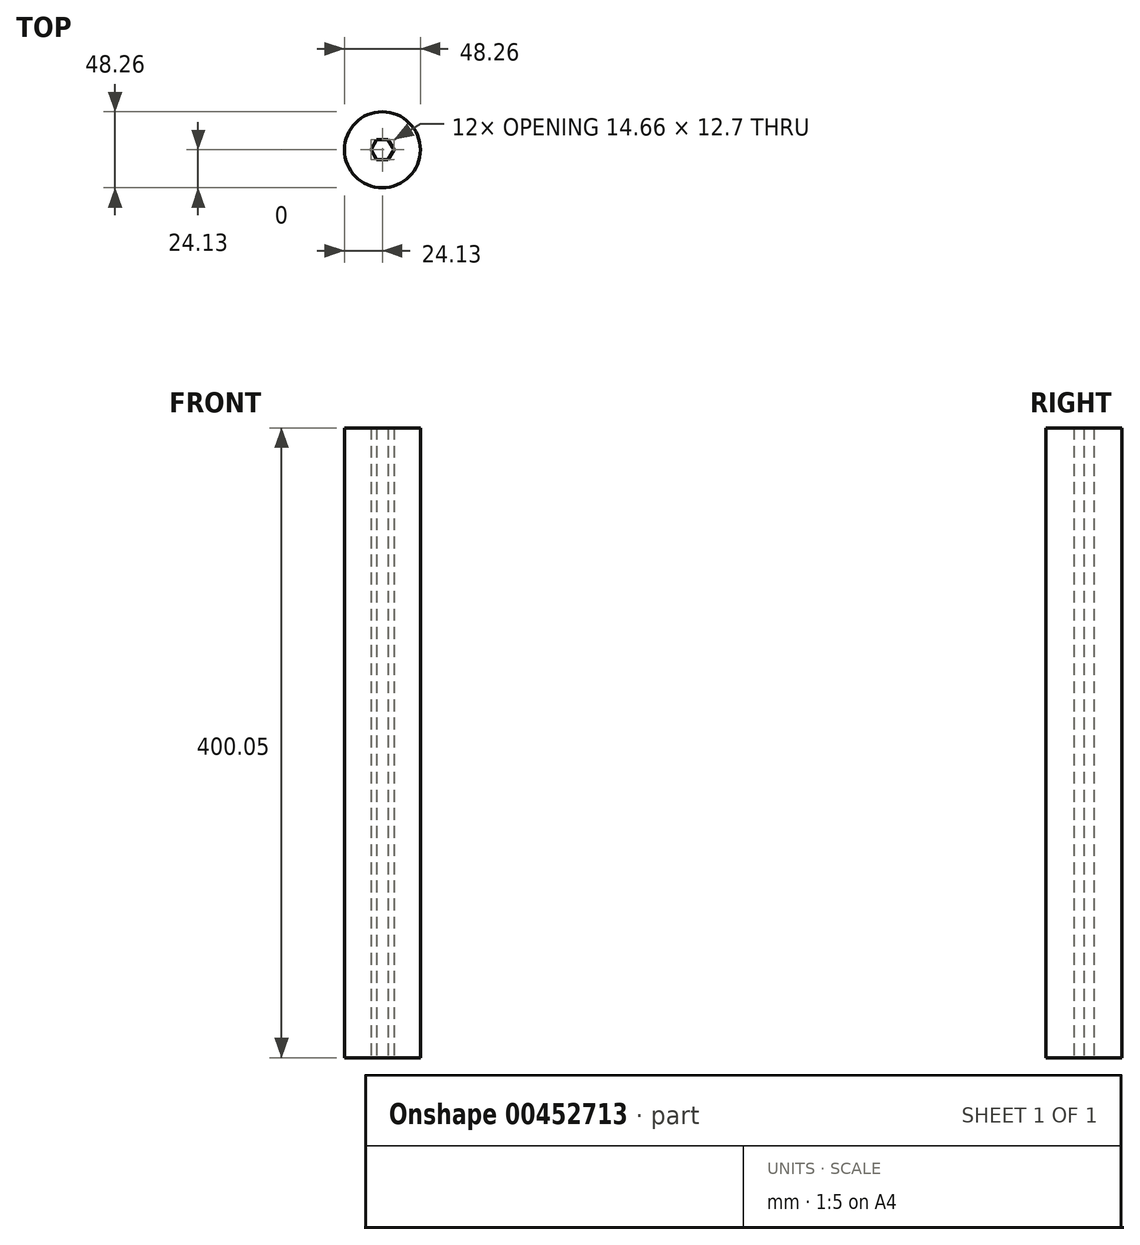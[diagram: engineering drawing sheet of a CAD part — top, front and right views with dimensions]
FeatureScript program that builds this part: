
annotation { "Feature Type Name" : "Feature", "Feature Type Description" : "" }
export const myFeature = defineFeature(function(context is Context, id is Id, definition is map)
    precondition{}
    {
        {
            var Q0;
            Q0=qCreatedBy(makeId("Top.planeOp"),FACE);
            var sketch = newSketch(context, id + "F0", { "sketchPlane" : qUnion([Q0])});
            skCircle(sketch, "E0", {"center": v(0, 0) * mm, "radius": 24.13 * mm});
            skCircle(sketch, "E1.cCircle", {"center": v(0, 0) * mm, "radius": 6.35 * mm, "construction": true});
            skLineSegment(sketch, "E1.0", {"start": v(-3.67, 6.35) * mm, "end": v(3.67, 6.35) * mm});
            skLineSegment(sketch, "E1.1", {"start": v(3.67, 6.35) * mm, "end": v(7.33, 0) * mm});
            skLineSegment(sketch, "E1.2", {"start": v(7.33, 0) * mm, "end": v(3.67, -6.35) * mm});
            skLineSegment(sketch, "E1.3", {"start": v(3.67, -6.35) * mm, "end": v(-3.67, -6.35) * mm});
            skLineSegment(sketch, "E1.4", {"start": v(-3.67, -6.35) * mm, "end": v(-7.33, 0) * mm});
            skLineSegment(sketch, "E1.5", {"start": v(-7.33, 0) * mm, "end": v(-3.67, 6.35) * mm});
            skPoint(sketch, "E1.0.midPoint", {"position": v(0, 6.35) * mm});
            skSolve(sketch);
        }
        {
            var Q0;
            Q0 = qSketchRegion(id + "F0", true);
            extrude(context, id + "F1", {"entities" : qUnion([Q0]), "depth" : 400.05 * mm, "offsetDistance" : 25.4 * mm});
        }
    });
